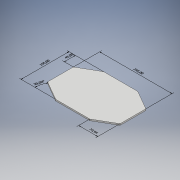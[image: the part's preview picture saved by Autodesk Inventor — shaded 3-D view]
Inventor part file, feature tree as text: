
AUTODESK INVENTOR PART (.ipt)
format: ipt  version: 2018 (Build 220112000, 112)  size: 124,416 bytes
history: native  units: mm
features: other x6, chamfer x2, extrude x1, sketch x1
ambient origin geometry x8: Origin, YZ Plane, XZ Plane, XY Plane, X Axis, Y Axis, Z Axis, Center Point
bodies: Solide1 (feature_tree)
feature tree (10):
  other  "Annotations"
  extrude  "Extrusion1"  Depth=295.0mm
  chamfer  "Chanfrein1"  Distance=195.0mm
  chamfer  "Chanfrein2"  Distance=6.0mm
  sketch  "Esquisse1"
  other  "Cote linéaire 1"
  other  "Cote linéaire 2"
  other  "Cote linéaire 3"
  other  "Cote linéaire 4"
  other  "Cote angulaire 1"
